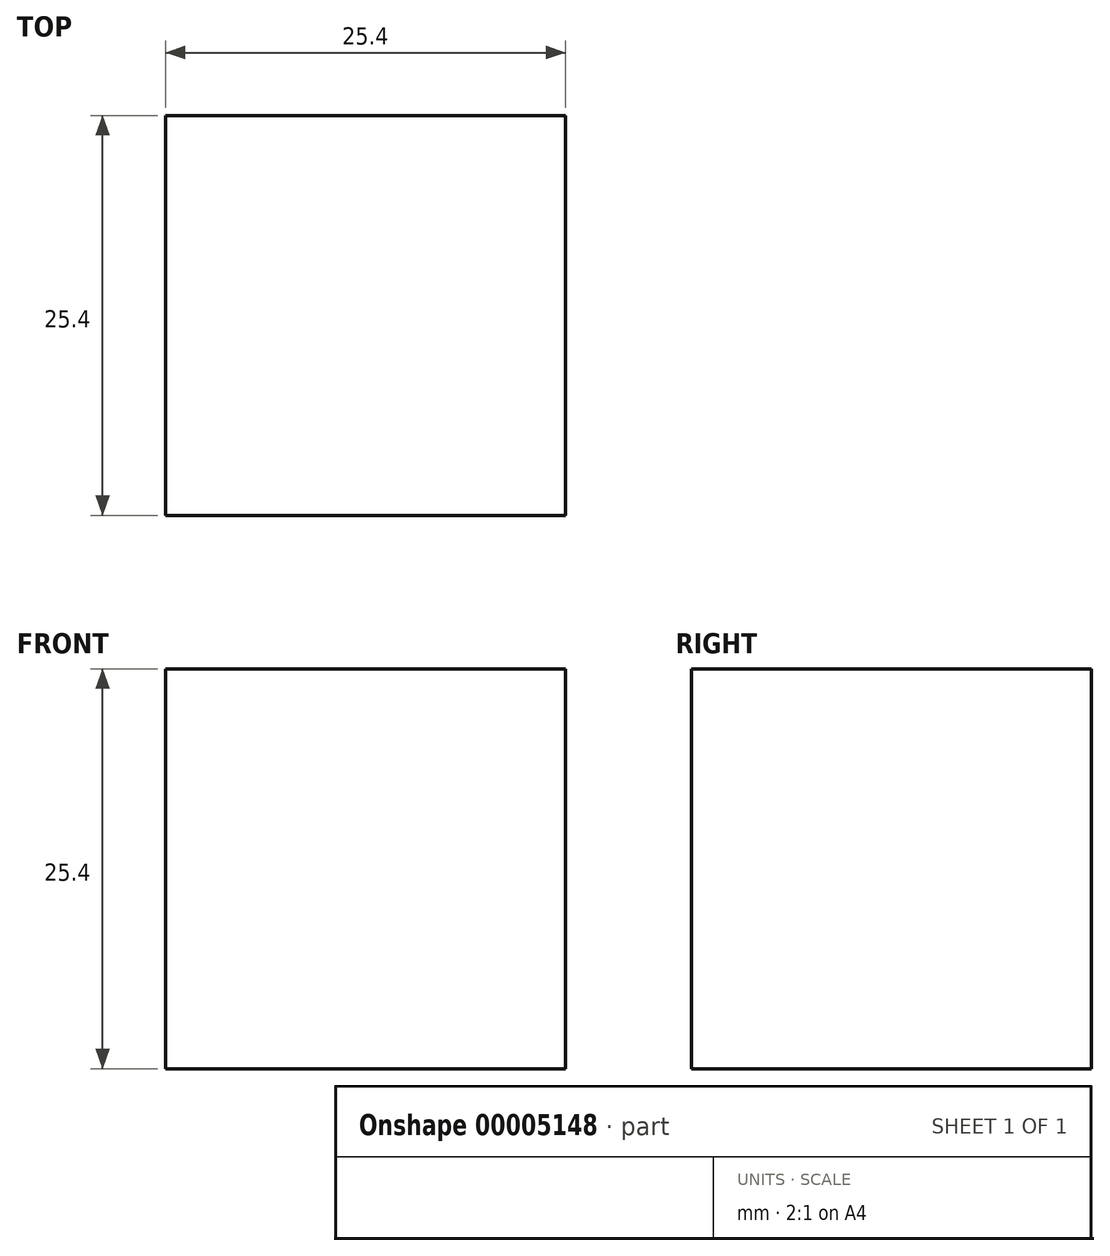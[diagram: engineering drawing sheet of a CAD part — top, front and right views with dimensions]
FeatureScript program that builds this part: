
annotation { "Feature Type Name" : "Feature", "Feature Type Description" : "" }
export const myFeature = defineFeature(function(context is Context, id is Id, definition is map)
    precondition{}
    {
        {
            var Q0;
            Q0=qCreatedBy(makeId("Front.planeOp"),FACE);
            var sketch = newSketch(context, id + "F0", { "sketchPlane" : qUnion([Q0])});
            skLineSegment(sketch, "E0.rect.bottom", {"start": v(12.7, -12.7) * mm, "end": v(-12.7, -12.7) * mm});
            skLineSegment(sketch, "E0.rect.top", {"start": v(12.7, 12.7) * mm, "end": v(-12.7, 12.7) * mm});
            skLineSegment(sketch, "E0.rect.left", {"start": v(12.7, -12.7) * mm, "end": v(12.7, 12.7) * mm});
            skLineSegment(sketch, "E0.rect.right", {"start": v(-12.7, -12.7) * mm, "end": v(-12.7, 12.7) * mm});
            skPoint(sketch, "E0.rect.middle", {"position": v(0, 0) * mm});
            skSolve(sketch);
        }
        {
            var Q0;
            Q0=makeQuery(id+"F0.imprint","IMPRINT",FACE,{"disambiguationData":[TD([[makeQuery(id+"F0.imprint","IMPRINT",EDGE,{"derivedFrom":sQuery(id+"F0.wireOp",EDGE,"E0.rect.bottom")}),-1.0]])]});
            extrude(context, id + "F1", {"entities" : qUnion([Q0]), "depth" : 25.4 * mm});
        }
    });
